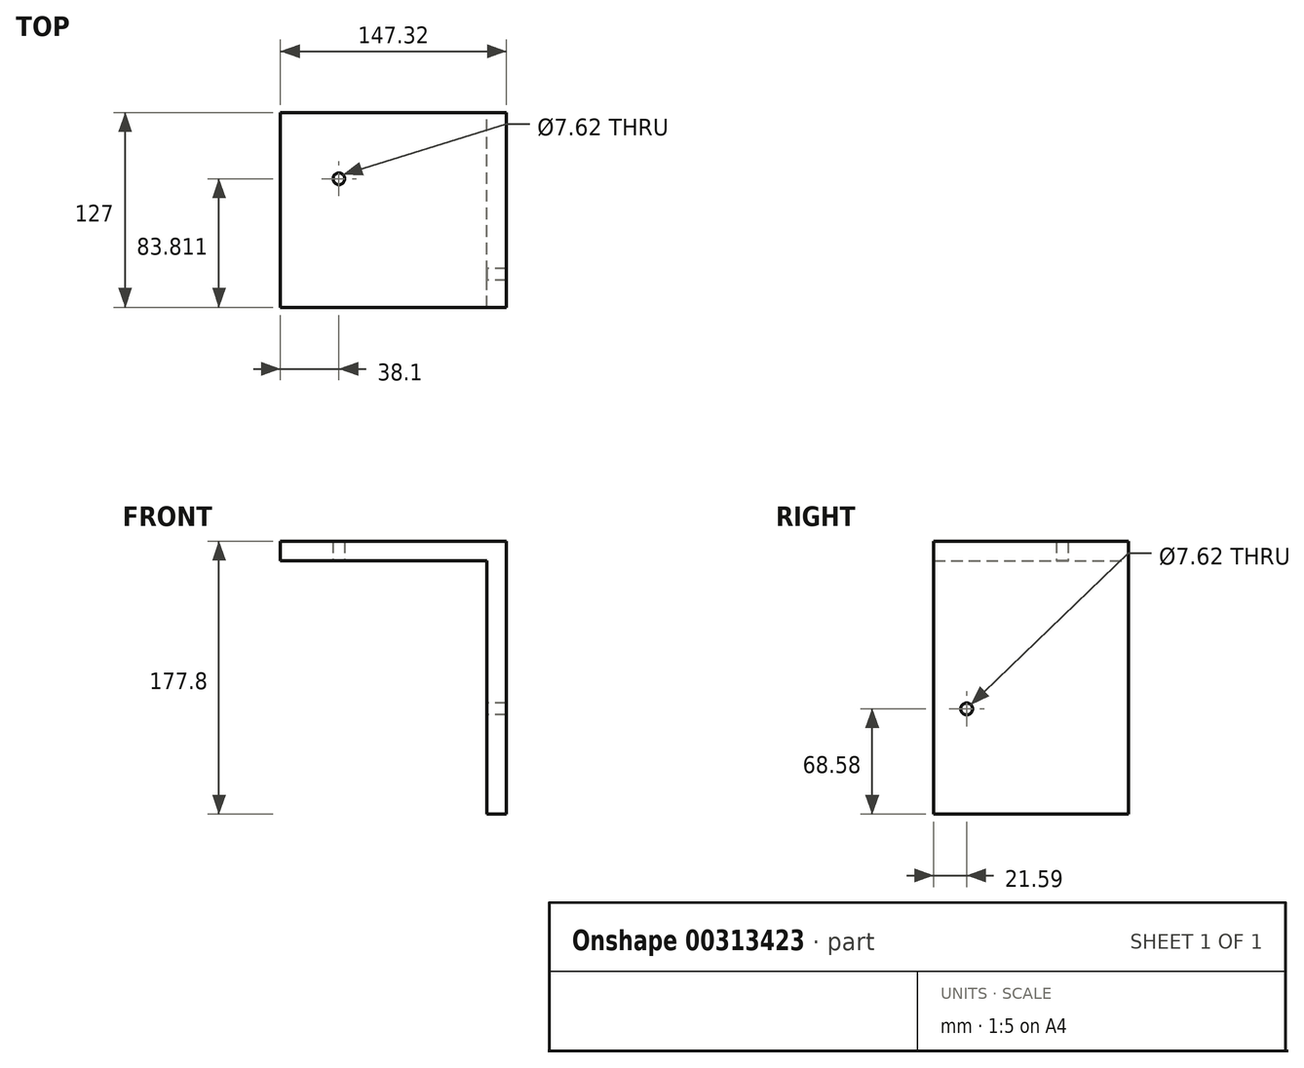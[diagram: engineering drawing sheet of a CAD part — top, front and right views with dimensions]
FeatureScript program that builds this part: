
annotation { "Feature Type Name" : "Feature", "Feature Type Description" : "" }
export const myFeature = defineFeature(function(context is Context, id is Id, definition is map)
    precondition{}
    {
        {
            var Q0;
            Q0=qCreatedBy(makeId("Front.planeOp"),FACE);
            var sketch = newSketch(context, id + "F0", { "sketchPlane" : qUnion([Q0])});
            skLineSegment(sketch, "E0", {"start": v(0, 0) * mm, "end": v(-134.62, 0) * mm});
            skLineSegment(sketch, "E1", {"start": v(-134.62, 0) * mm, "end": v(-134.62, 12.7) * mm});
            skLineSegment(sketch, "E2", {"start": v(-134.62, 12.7) * mm, "end": v(12.7, 12.7) * mm});
            skLineSegment(sketch, "E3", {"start": v(12.7, 12.7) * mm, "end": v(12.7, -165.1) * mm});
            skLineSegment(sketch, "E4", {"start": v(12.7, -165.1) * mm, "end": v(0, -165.1) * mm});
            skLineSegment(sketch, "E5", {"start": v(0, -165.1) * mm, "end": v(0, 0) * mm});
            skSolve(sketch);
        }
        {
            var Q0;
            Q0 = qSketchRegion(id + "F0", true);
            extrude(context, id + "F1", {"entities" : qUnion([Q0]), "depth" : 127 * mm});
        }
        {
            var Q0;
            Q0=makeQuery(id+"F1.opExtrude","SWEPT_FACE",FACE,{"disambiguationData":[OSD([sQuery(id+"F0.wireOp",EDGE,"E0")])]});
            var sketch = newSketch(context, id + "F2", { "sketchPlane" : qUnion([Q0])});
            skLineSegment(sketch, "E6", {"start": v(-134.62, 0) * mm, "end": v(-134.62, -3.56) * mm});
            skCircle(sketch, "E7", {"center": v(-96.52, 43.19) * mm, "radius": 3.81 * mm});
            skSolve(sketch);
        }
        {
            var Q0;
            Q0 = qSketchRegion(id + "F2", true);
            extrude(context, id + "F3", {"entities" : qUnion([Q0]), "operationType" : NewBodyOperationType.REMOVE, "oppositeDirection" : true, "depth" : 25.4 * mm});
        }
        {
            var Q0;
            Q0=makeQuery(id+"F1.opExtrude","SWEPT_FACE",FACE,{"disambiguationData":[OSD([sQuery(id+"F0.wireOp",EDGE,"E5")])]});
            var sketch = newSketch(context, id + "F4", { "sketchPlane" : qUnion([Q0])});
            skLineSegment(sketch, "E8", {"start": v(127, -165.1) * mm, "end": v(105.4, -165.1) * mm});
            skLineSegment(sketch, "E9", {"start": v(105.4, -165.1) * mm, "end": v(105.4, -96.52) * mm, "construction": true});
            skCircle(sketch, "E10", {"center": v(105.4, -96.52) * mm, "radius": 3.81 * mm});
            skSolve(sketch);
        }
        {
            var Q0;
            Q0=makeQuery(id+"F4.imprint","IMPRINT",FACE,{"disambiguationData":[TD([[makeQuery(id+"F4.imprint","IMPRINT",EDGE,{"derivedFrom":sQuery(id+"F4.wireOp",EDGE,"E10")}),1.0]])]});
            var Q1;
            Q1=sQuery(id+"F4.wireOp",EDGE,"E9");
            var Q2;
            Q2=sQuery(id+"F4.wireOp",EDGE,"E10");
            extrude(context, id + "F5", {"entities" : qUnion([Q0]), "operationType" : NewBodyOperationType.REMOVE, "surfaceEntities" : qUnion([Q1, Q2]), "oppositeDirection" : true, "depth" : 25.4 * mm});
        }
    });
